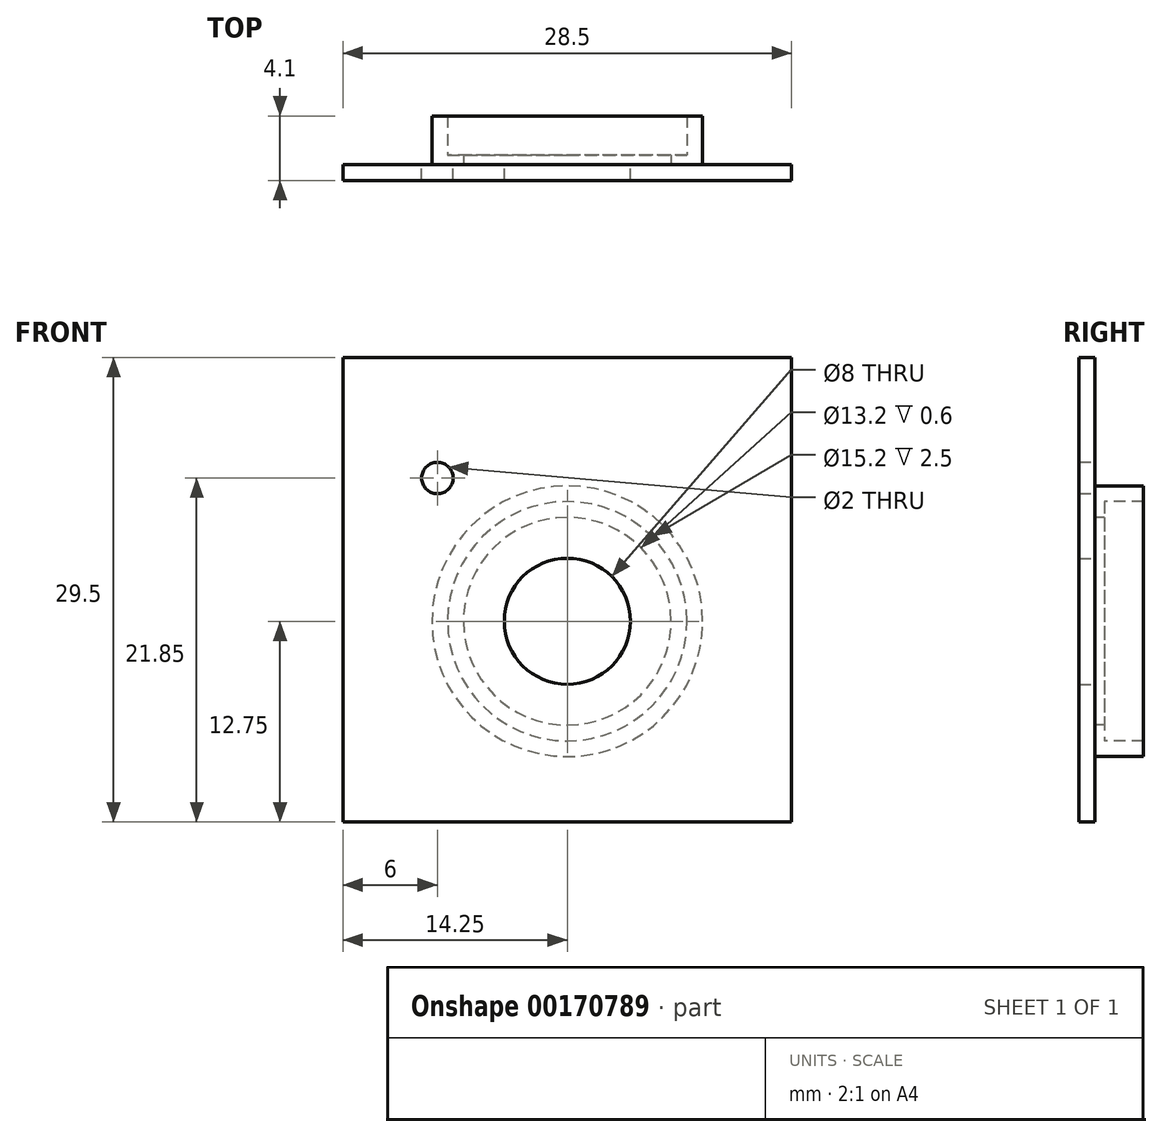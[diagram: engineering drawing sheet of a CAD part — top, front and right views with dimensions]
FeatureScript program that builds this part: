
annotation { "Feature Type Name" : "Feature", "Feature Type Description" : "" }
export const myFeature = defineFeature(function(context is Context, id is Id, definition is map)
    precondition{}
    {
        {
            var Q0;
            Q0=qCreatedBy(makeId("Front.planeOp"),FACE);
            var sketch = newSketch(context, id + "F0", { "sketchPlane" : qUnion([Q0])});
            skLineSegment(sketch, "E0.bottom", {"start": v(-14.25, 16.75) * mm, "end": v(14.25, 16.75) * mm});
            skLineSegment(sketch, "E0.top", {"start": v(-14.25, -12.75) * mm, "end": v(14.25, -12.75) * mm});
            skLineSegment(sketch, "E0.left", {"start": v(-14.25, 16.75) * mm, "end": v(-14.25, -12.75) * mm});
            skLineSegment(sketch, "E0.right", {"start": v(14.25, 16.75) * mm, "end": v(14.25, -12.75) * mm});
            skLineSegment(sketch, "E1.bottom", {"start": v(-12.5, 14) * mm, "end": v(12.5, 14) * mm, "construction": true});
            skLineSegment(sketch, "E1.top", {"start": v(-12.5, -10) * mm, "end": v(12.5, -10) * mm, "construction": true});
            skLineSegment(sketch, "E1.left", {"start": v(-12.5, 14) * mm, "end": v(-12.5, -10) * mm, "construction": true});
            skLineSegment(sketch, "E1.right", {"start": v(12.5, 14) * mm, "end": v(12.5, -10) * mm, "construction": true});
            skLineSegment(sketch, "E2", {"start": v(0, 14) * mm, "end": v(0, -10) * mm, "construction": true});
            skLineSegment(sketch, "E3", {"start": v(-12.5, 2) * mm, "end": v(12.5, 2) * mm, "construction": true});
            skLineSegment(sketch, "E4", {"start": v(-12.5, 0) * mm, "end": v(12.5, 0) * mm, "construction": true});
            skLineSegment(sketch, "E5", {"start": v(0, 16.75) * mm, "end": v(0, -12.75) * mm, "construction": true});
            skLineSegment(sketch, "E6", {"start": v(-14.25, 2) * mm, "end": v(14.25, 2) * mm, "construction": true});
            skSolve(sketch);
        }
        {
            var Q0;
            Q0 = qSketchRegion(id + "F0", true);
            extrude(context, id + "F1", {"entities" : qUnion([Q0]), "depth" : 1 * mm});
        }
        {
            var Q0;
            Q0=makeQuery(id+"F1.opExtrude","CAP_FACE",FACE,{"disambiguationData":[OSD([sQuery(id+"F0.wireOp",EDGE,"E0.bottom"),sQuery(id+"F0.wireOp",EDGE,"E0.top"),sQuery(id+"F0.wireOp",EDGE,"E0.left"),sQuery(id+"F0.wireOp",EDGE,"E0.right")])],"isStart":false});
            var sketch = newSketch(context, id + "F2", { "sketchPlane" : qUnion([Q0])});
            skLineSegment(sketch, "E7.bottom", {"start": v(12.75, 14.1) * mm, "end": v(-12.75, 14.1) * mm});
            skLineSegment(sketch, "E7.top", {"start": v(12.75, -10.1) * mm, "end": v(-12.75, -10.1) * mm});
            skLineSegment(sketch, "E7.left", {"start": v(12.75, 14.1) * mm, "end": v(12.75, -10.1) * mm});
            skLineSegment(sketch, "E7.right", {"start": v(-12.75, 14.1) * mm, "end": v(-12.75, -10.1) * mm});
            skLineSegment(sketch, "E8", {"start": v(0, 14.1) * mm, "end": v(0, -10.1) * mm, "construction": true});
            skLineSegment(sketch, "E9", {"start": v(12.75, 2) * mm, "end": v(-12.75, 2) * mm, "construction": true});
            skLineSegment(sketch, "E10", {"start": v(14.25, 2) * mm, "end": v(-14.25, 2) * mm, "construction": true});
            skSolve(sketch);
        }
        {
            var Q0;
            Q0=qCreatedBy(makeId("Front.planeOp"),FACE);
            var sketch = newSketch(context, id + "F3", { "sketchPlane" : qUnion([Q0])});
            skCircle(sketch, "E11", {"center": v(0, 0) * mm, "radius": 4 * mm});
            skSolve(sketch);
        }
        {
            var Q0;
            Q0 = qSketchRegion(id + "F3", true);
            extrude(context, id + "F4", {"entities" : qUnion([Q0]), "operationType" : NewBodyOperationType.REMOVE, "depth" : 25 * mm});
        }
        {
            var Q0;
            Q0=makeQuery(id+"F1.opExtrude","CAP_FACE",FACE,{"disambiguationData":[OSD([sQuery(id+"F0.wireOp",EDGE,"E0.bottom"),sQuery(id+"F0.wireOp",EDGE,"E0.top"),sQuery(id+"F0.wireOp",EDGE,"E0.left"),sQuery(id+"F0.wireOp",EDGE,"E0.right")])],"isStart":true});
            var sketch = newSketch(context, id + "F5", { "sketchPlane" : qUnion([Q0])});
            skCircle(sketch, "E12", {"center": v(0, 0) * mm, "radius": 6.6 * mm});
            skCircle(sketch, "E13", {"center": v(0, 0) * mm, "radius": 8.6 * mm});
            skSolve(sketch);
        }
        {
            var Q0;
            Q0 = qSketchRegion(id + "F5", true);
            extrude(context, id + "F6", {"entities" : qUnion([Q0]), "operationType" : NewBodyOperationType.ADD, "depth" : 0.6 * mm});
        }
        {
            var Q0;
            Q0=makeQuery(id+"F6.opExtrude","CAP_FACE",FACE,{"disambiguationData":[OSD([sQuery(id+"F5.wireOp",EDGE,"E12"),sQuery(id+"F5.wireOp",EDGE,"E13")])],"isStart":false});
            var sketch = newSketch(context, id + "F7", { "sketchPlane" : qUnion([Q0])});
            skCircle(sketch, "E14", {"center": v(0, 0) * mm, "radius": 8.6 * mm});
            skCircle(sketch, "E15", {"center": v(0, 0) * mm, "radius": 7.6 * mm});
            skSolve(sketch);
        }
        {
            var Q0;
            Q0 = qSketchRegion(id + "F7", true);
            extrude(context, id + "F8", {"entities" : qUnion([Q0]), "operationType" : NewBodyOperationType.ADD, "depth" : 2.5 * mm});
        }
        {
            var Q0;
            {var subQ0=sQuery(id+"F0.wireOp",EDGE,"E0.right");var subQ1=sQuery(id+"F0.wireOp",EDGE,"E0.left");var subQ2=sQuery(id+"F0.wireOp",EDGE,"E0.top");var subQ3=sQuery(id+"F0.wireOp",EDGE,"E0.bottom");Q0=makeQuery(id+"F6.boolean.opBoolean","SPLIT",FACE,{"disambiguationData":[TD([makeQuery(id+"F1.opExtrude","SWEPT_FACE",FACE,{"disambiguationData":[OSD([subQ3])]})])],"derivedFrom":makeQuery(id+"F1.opExtrude","CAP_FACE",FACE,{"disambiguationData":[OSD([subQ3,subQ2,subQ1,subQ0])],"isStart":true})});}
            var sketch = newSketch(context, id + "F9", { "sketchPlane" : qUnion([Q0])});
            skCircle(sketch, "E16", {"center": v(8.25, 9.1) * mm, "radius": 1 * mm});
            skSolve(sketch);
        }
        {
            var Q0;
            Q0 = qSketchRegion(id + "F9", true);
            extrude(context, id + "F10", {"entities" : qUnion([Q0]), "operationType" : NewBodyOperationType.REMOVE, "oppositeDirection" : true, "depth" : 25 * mm});
        }
    });
